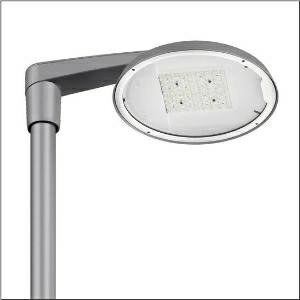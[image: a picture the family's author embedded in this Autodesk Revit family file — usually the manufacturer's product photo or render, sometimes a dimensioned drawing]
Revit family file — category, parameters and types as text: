
# Revit family: dl_50_iq_mini___st0_5a_5xa248b41f08le_5a74
name_source: partatom
category: Lighting Fixtures
units: mm (PartAtom-declared; Revit-internal decimal feet)

## family parameters
Cut with Voids When Loaded = No
Host = Face
Light Source = No
Part Type = Normal
Room Calculation Point = No
Round Connector Dimension = Use Diameter
Shared = No

## types (1)
- --- (1 x LED, 10390 lm, 64.1 W, 4000K)
    Apparent Load = 64 VA
    CIE Flux Codes = 41 75 97 100 100
    Color Rendering = 70
    Color Temperature = 4000K
    Default Elevation = 1800 mm
    Description = DL 50 iQ mini, mast luminaire, primary light control with lens, of PMMA, primary optical cover: cover, of toughened safety glass, transparent, light distribution: ST0.5a, light emission: direct distribution, primary light characteristic: asymmetric, installation type: side-entry, post-top, LED, High Power LED, rated luminous flux: 10.390lm, luminous efficacy: 162lm/W, light colour: 740, colour temperature: 4000K, control gear: iQ Street-Remote, control: optimised constant luminous flux control (CLO 2.0), Desk-Remote (wireless, voltage-free reading and setting of iQ features in the workshop via application-optimized NFC function/RFID function), Light-Fading, Smart-Wire, Night-Set, Lumen-Switch, Temp-Guard, Auto-Match, Street-Remote, mains connection: 230..240V, AC, 50/60Hz, connection cable pre-assembled, cable length: 8,5m, start of lifetime: 64W, end of service life: 67W, reduction: 30W, luminaire housing, of diecast aluminium, powder-coated, SITECO metallic grey (DB 702S), inclination adjustable: 0°, 5°, 10° (post-top) | 0°, -5°, -10°, -15° (side-entry), please order mast post-top element or mast side-entry element separately, diameter: 500mm, height: 115mm, post-top: for spigot size d x l = 76 x 100mm; with reducer (optional accessory) 60 x 100mm | side-entry: for spigot size d x l = 60 x 100mm; with reducer (optional accessory) 42 x 100mm, mounting height: 4..6m, protection rating (complete): IP66, insulation class (complete): insulation class II (safety insulation), certification: CE, ENEC, ENEC+, VDE, impact resistance: IK08, permissible operating ambient temperature for outdoor applications: -25..+40°C, standard-compliant lighting for roads and squares, packaging unit: 1 piece

Light Distribution: ST0.5a
    Height = 115 mm
    Lamp = 1 x LED
    Lamp Light Flux = 10390 lm
    Lamp Power = 64.1 W
    Lamp count = 1
    Length = 500 mm
    Luminous efficacy = 162 lm/W
    Manufacturer = Siteco
    ModVariant = No
    Model = 5XA248B41F08LE
    Number of Poles = 1
    OnlyDefault = Yes
    Power Factor = 1
    Product Name = DL 50 iQ mini | ST0.5a
    Product group = mast luminaire | pylon top
    ProductGroupID = 6100
    Protection Class = Protection class II
    Protection Degree = IP 66
    RLX_Detail_Level = 1
    RLX_Emergency_Light_Flux = 0 lm
    RLX_Emergency_Type = 0
    RLX_Emergency_Type_DB = No
    RlxData = <blob elided: 127769 chars, md5=4ede2491>
    Socket = socket
    Standby Power = 0 W
    System Light Flux = 10390 lm
    System Power = 64 W
    Type Comments = factory setting: luminous flux: 100 % | dim-lin: 254 | 672 mA
    Type Image = l_1251790.jpg
    URL = http://relux.com
    VarID = @adj_142605
    Voltage = 0 V
    Weight = 0.00 kg
    Width = 0 mm  [stored 0 ft]

note: [stored X ft] marks values corroborated as IEEE doubles in the binary element streams (Revit-internal decimal feet)

## geometry (parser evidence)
native form markers: Blend x4, Sweep x12
no freeform markers — native parametric forms only
